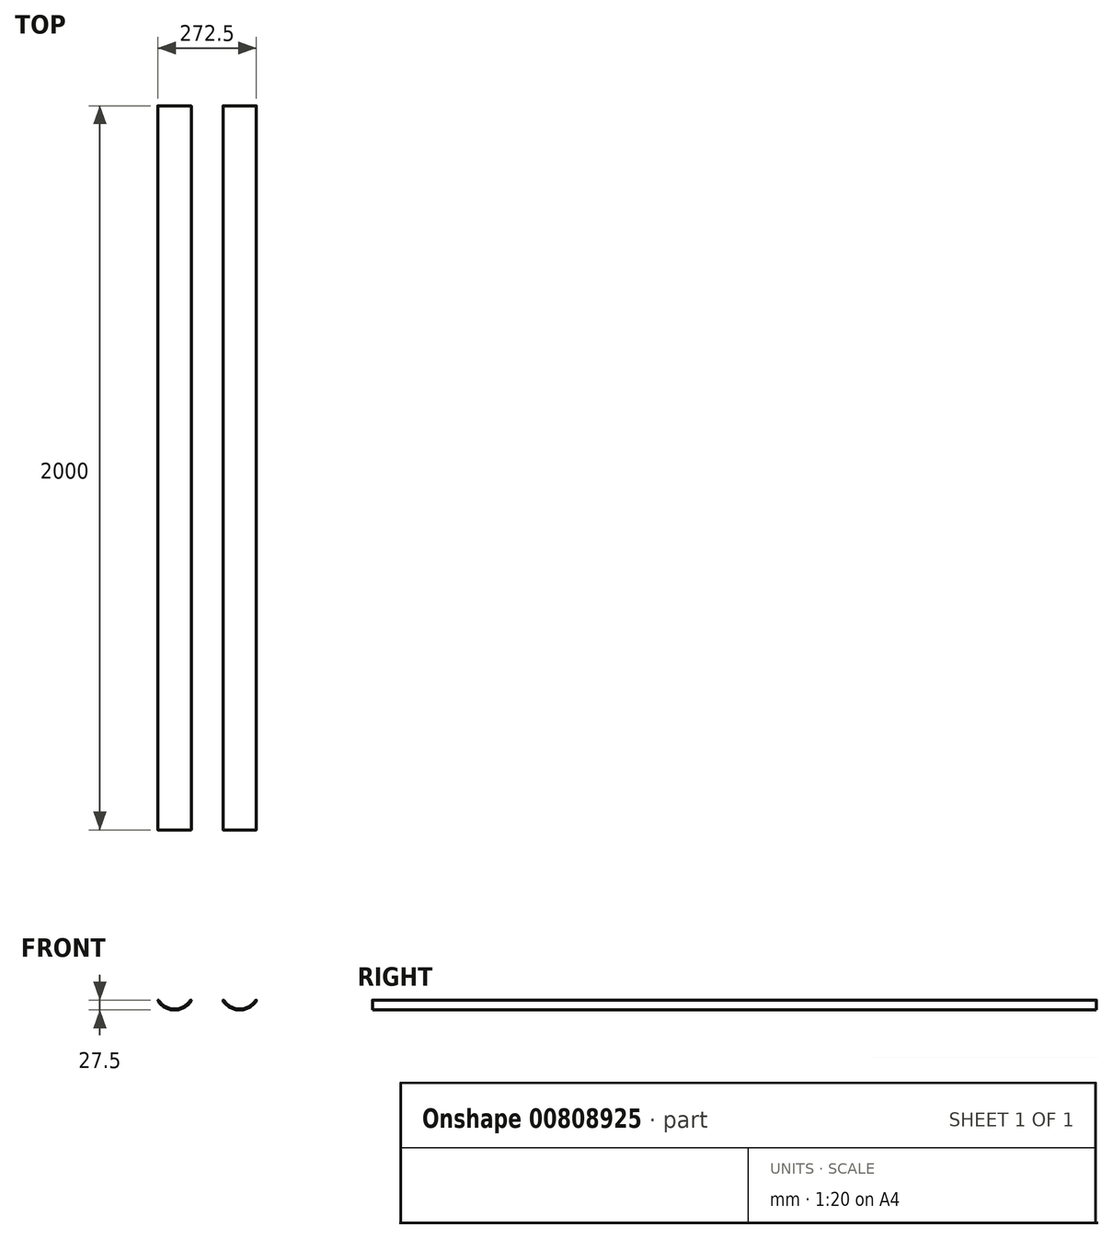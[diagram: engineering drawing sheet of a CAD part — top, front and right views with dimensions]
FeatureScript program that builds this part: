
annotation { "Feature Type Name" : "Feature", "Feature Type Description" : "" }
export const myFeature = defineFeature(function(context is Context, id is Id, definition is map)
    precondition{}
    {
        {
            var Q0;
            Q0=qCreatedBy(makeId("Front.planeOp"),FACE);
            var sketch = newSketch(context, id + "F0", { "sketchPlane" : qUnion([Q0])});
            skArc(sketch, "E0", {"start": v(0, 0) * mm, "mid": v(-45, 25) * mm, "end": v(-90, 0) * mm});
            skArc(sketch, "E1", {"start": v(0, 0) * mm, "mid": v(45, -25) * mm, "end": v(90, 0) * mm});
            skArc(sketch, "E2.1.0.0", {"start": v(180, 0) * mm, "mid": v(135, 25) * mm, "end": v(90, 0) * mm});
            skArc(sketch, "E2.1.0.1", {"start": v(180, 0) * mm, "mid": v(135, 25) * mm, "end": v(90, 0) * mm});
            skArc(sketch, "E2.1.0.2", {"start": v(180, 0) * mm, "mid": v(225, -25) * mm, "end": v(270, 0) * mm});
            skArc(sketch, "E2.2.0.0", {"start": v(360, 0) * mm, "mid": v(315, 25) * mm, "end": v(270, 0) * mm});
            skArc(sketch, "E2.2.0.1", {"start": v(360, 0) * mm, "mid": v(315, 25) * mm, "end": v(270, 0) * mm});
            skArc(sketch, "E2.2.0.2", {"start": v(360, 0) * mm, "mid": v(405, -25) * mm, "end": v(450, 0) * mm});
            skArc(sketch, "E2.3.0.0", {"start": v(540, 0) * mm, "mid": v(495, 25) * mm, "end": v(450, 0) * mm});
            skArc(sketch, "E2.3.0.1", {"start": v(540, 0) * mm, "mid": v(495, 25) * mm, "end": v(450, 0) * mm});
            skArc(sketch, "E3", {"start": v(-97.5, -9.45) * mm, "mid": v(-93.48, -4.94) * mm, "end": v(-90, 0) * mm});
            skPoint(sketch, "E4.orphan", {"position": v(900, 0) * mm});
            skArc(sketch, "E5.0.startCap", {"start": v(181.06, 0.66) * mm, "mid": v(180.66, -1.06) * mm, "end": v(178.94, -0.66) * mm});
            skArc(sketch, "E5.0.endCap", {"start": v(91.06, -0.66) * mm, "mid": v(89.34, -1.06) * mm, "end": v(88.94, 0.66) * mm});
            skArc(sketch, "E5.0.left", {"start": v(178.94, -0.66) * mm, "mid": v(135, 23.75) * mm, "end": v(91.06, -0.66) * mm});
            skArc(sketch, "E5.0.right", {"start": v(181.06, 0.66) * mm, "mid": v(135, 26.25) * mm, "end": v(88.94, 0.66) * mm});
            skArc(sketch, "E5.1.startCap", {"start": v(178.94, -0.66) * mm, "mid": v(179.34, 1.06) * mm, "end": v(181.06, 0.66) * mm});
            skArc(sketch, "E5.1.endCap", {"start": v(268.94, 0.66) * mm, "mid": v(270.66, 1.06) * mm, "end": v(271.06, -0.66) * mm});
            skArc(sketch, "E5.1.left", {"start": v(181.06, 0.66) * mm, "mid": v(225, -23.75) * mm, "end": v(268.94, 0.66) * mm});
            skArc(sketch, "E5.1.right", {"start": v(178.94, -0.66) * mm, "mid": v(225, -26.25) * mm, "end": v(271.06, -0.66) * mm});
            skArc(sketch, "E5.2.startCap", {"start": v(-1.06, -0.66) * mm, "mid": v(-0.66, 1.06) * mm, "end": v(1.06, 0.66) * mm});
            skArc(sketch, "E5.2.endCap", {"start": v(88.94, 0.66) * mm, "mid": v(90.66, 1.06) * mm, "end": v(91.06, -0.66) * mm});
            skArc(sketch, "E5.2.left", {"start": v(1.06, 0.66) * mm, "mid": v(45, -23.75) * mm, "end": v(88.94, 0.66) * mm});
            skArc(sketch, "E5.2.right", {"start": v(-1.06, -0.66) * mm, "mid": v(45, -26.25) * mm, "end": v(91.06, -0.66) * mm});
            skArc(sketch, "E5.3.startCap", {"start": v(538.94, -0.66) * mm, "mid": v(539.34, 1.06) * mm, "end": v(541.06, 0.66) * mm});
            skArc(sketch, "E5.5.startCap", {"start": v(541.06, 0.66) * mm, "mid": v(540.66, -1.06) * mm, "end": v(538.94, -0.66) * mm});
            skArc(sketch, "E5.5.endCap", {"start": v(451.06, -0.66) * mm, "mid": v(449.34, -1.06) * mm, "end": v(448.94, 0.66) * mm});
            skArc(sketch, "E5.5.left", {"start": v(538.94, -0.66) * mm, "mid": v(495, 23.75) * mm, "end": v(451.06, -0.66) * mm});
            skArc(sketch, "E5.5.right", {"start": v(541.06, 0.66) * mm, "mid": v(495, 26.25) * mm, "end": v(448.94, 0.66) * mm});
            skArc(sketch, "E5.6.startCap", {"start": v(-96.62, -10.34) * mm, "mid": v(-98.38, -10.34) * mm, "end": v(-98.38, -8.57) * mm});
            skArc(sketch, "E5.6.endCap", {"start": v(-91.06, 0.66) * mm, "mid": v(-89.34, 1.06) * mm, "end": v(-88.94, -0.66) * mm});
            skArc(sketch, "E5.6.left", {"start": v(-98.38, -8.57) * mm, "mid": v(-94.46, -4.16) * mm, "end": v(-91.06, 0.66) * mm});
            skArc(sketch, "E5.6.right", {"start": v(-96.62, -10.34) * mm, "mid": v(-92.5, -5.72) * mm, "end": v(-88.94, -0.66) * mm});
            skArc(sketch, "E5.7.startCap", {"start": v(1.06, 0.66) * mm, "mid": v(0.66, -1.06) * mm, "end": v(-1.06, -0.66) * mm});
            skArc(sketch, "E5.7.endCap", {"start": v(-88.94, -0.66) * mm, "mid": v(-90.66, -1.06) * mm, "end": v(-91.06, 0.66) * mm});
            skArc(sketch, "E5.7.left", {"start": v(-1.06, -0.66) * mm, "mid": v(-45, 23.75) * mm, "end": v(-88.94, -0.66) * mm});
            skArc(sketch, "E5.7.right", {"start": v(1.06, 0.66) * mm, "mid": v(-45, 26.25) * mm, "end": v(-91.06, 0.66) * mm});
            skArc(sketch, "E5.10.startCap", {"start": v(358.94, -0.66) * mm, "mid": v(359.34, 1.06) * mm, "end": v(361.06, 0.66) * mm});
            skArc(sketch, "E5.10.endCap", {"start": v(448.94, 0.66) * mm, "mid": v(450.66, 1.06) * mm, "end": v(451.06, -0.66) * mm});
            skArc(sketch, "E5.10.left", {"start": v(361.06, 0.66) * mm, "mid": v(405, -23.75) * mm, "end": v(448.94, 0.66) * mm});
            skArc(sketch, "E5.10.right", {"start": v(358.94, -0.66) * mm, "mid": v(405, -26.25) * mm, "end": v(451.06, -0.66) * mm});
            skArc(sketch, "E5.11.startCap", {"start": v(361.06, 0.66) * mm, "mid": v(360.66, -1.06) * mm, "end": v(358.94, -0.66) * mm});
            skArc(sketch, "E5.11.endCap", {"start": v(271.06, -0.66) * mm, "mid": v(269.34, -1.06) * mm, "end": v(268.94, 0.66) * mm});
            skArc(sketch, "E5.11.left", {"start": v(358.94, -0.66) * mm, "mid": v(315, 23.75) * mm, "end": v(271.06, -0.66) * mm});
            skArc(sketch, "E5.11.right", {"start": v(361.06, 0.66) * mm, "mid": v(315, 26.25) * mm, "end": v(268.94, 0.66) * mm});
            skArc(sketch, "E5.12.startCap", {"start": v(-1.06, -0.66) * mm, "mid": v(-0.66, 1.06) * mm, "end": v(1.06, 0.66) * mm});
            skArc(sketch, "E5.12.endCap", {"start": v(88.94, 0.66) * mm, "mid": v(90.66, 1.06) * mm, "end": v(91.06, -0.66) * mm});
            skArc(sketch, "E5.12.left", {"start": v(1.06, 0.66) * mm, "mid": v(45, -23.75) * mm, "end": v(88.94, 0.66) * mm});
            skArc(sketch, "E5.12.right", {"start": v(-1.06, -0.66) * mm, "mid": v(45, -26.25) * mm, "end": v(91.06, -0.66) * mm});
            skArc(sketch, "E5.13.startCap", {"start": v(181.06, 0.66) * mm, "mid": v(180.66, -1.06) * mm, "end": v(178.94, -0.66) * mm});
            skArc(sketch, "E5.13.endCap", {"start": v(91.06, -0.66) * mm, "mid": v(89.34, -1.06) * mm, "end": v(88.94, 0.66) * mm});
            skArc(sketch, "E5.13.left", {"start": v(178.94, -0.66) * mm, "mid": v(135, 23.75) * mm, "end": v(91.06, -0.66) * mm});
            skArc(sketch, "E5.13.right", {"start": v(181.06, 0.66) * mm, "mid": v(135, 26.25) * mm, "end": v(88.94, 0.66) * mm});
            skArc(sketch, "E5.14.startCap", {"start": v(1.06, 0.66) * mm, "mid": v(0.66, -1.06) * mm, "end": v(-1.06, -0.66) * mm});
            skArc(sketch, "E5.14.endCap", {"start": v(-88.94, -0.66) * mm, "mid": v(-90.66, -1.06) * mm, "end": v(-91.06, 0.66) * mm});
            skArc(sketch, "E5.14.left", {"start": v(-1.06, -0.66) * mm, "mid": v(-45, 23.75) * mm, "end": v(-88.94, -0.66) * mm});
            skArc(sketch, "E5.14.right", {"start": v(1.06, 0.66) * mm, "mid": v(-45, 26.25) * mm, "end": v(-91.06, 0.66) * mm});
            skArc(sketch, "E5.15.startCap", {"start": v(541.06, 0.66) * mm, "mid": v(540.66, -1.06) * mm, "end": v(538.94, -0.66) * mm});
            skArc(sketch, "E5.15.endCap", {"start": v(451.06, -0.66) * mm, "mid": v(449.34, -1.06) * mm, "end": v(448.94, 0.66) * mm});
            skArc(sketch, "E5.15.left", {"start": v(538.94, -0.66) * mm, "mid": v(495, 23.75) * mm, "end": v(451.06, -0.66) * mm});
            skArc(sketch, "E5.15.right", {"start": v(541.06, 0.66) * mm, "mid": v(495, 26.25) * mm, "end": v(448.94, 0.66) * mm});
            skArc(sketch, "E5.17.startCap", {"start": v(361.06, 0.66) * mm, "mid": v(360.66, -1.06) * mm, "end": v(358.94, -0.66) * mm});
            skArc(sketch, "E5.17.endCap", {"start": v(271.06, -0.66) * mm, "mid": v(269.34, -1.06) * mm, "end": v(268.94, 0.66) * mm});
            skArc(sketch, "E5.17.left", {"start": v(358.94, -0.66) * mm, "mid": v(315, 23.75) * mm, "end": v(271.06, -0.66) * mm});
            skArc(sketch, "E5.17.right", {"start": v(361.06, 0.66) * mm, "mid": v(315, 26.25) * mm, "end": v(268.94, 0.66) * mm});
            skSolve(sketch);
        }
        {
            var Q0;
            {var subQ5=sQuery(id+"F0.wireOp",EDGE,"E5.17.left");Q0=makeQuery(id+"F0.imprint","IMPRINT",FACE,{"disambiguationData":[TD([[makeQuery(id+"F0.imprint","IMPRINT",EDGE,{"derivedFrom":subQ5}),-1.0]])]});}
            var Q1;
            {var subQ5=sQuery(id+"F0.wireOp",EDGE,"E5.14.left");Q1=makeQuery(id+"F0.imprint","IMPRINT",FACE,{"disambiguationData":[TD([[makeQuery(id+"F0.imprint","IMPRINT",EDGE,{"derivedFrom":subQ5}),-1.0]])]});}
            var Q2;
            {var subQ5=sQuery(id+"F0.wireOp",EDGE,"E5.1.left");Q2=makeQuery(id+"F0.imprint","IMPRINT",FACE,{"disambiguationData":[TD([[makeQuery(id+"F0.imprint","IMPRINT",EDGE,{"derivedFrom":subQ5}),-1.0]])]});}
            var Q3;
            {var subQ5=sQuery(id+"F0.wireOp",EDGE,"E5.13.right");Q3=makeQuery(id+"F0.imprint","IMPRINT",FACE,{"disambiguationData":[TD([[makeQuery(id+"F0.imprint","IMPRINT",EDGE,{"derivedFrom":subQ5}),1.0]])]});}
            var Q4;
            {var subQ5=sQuery(id+"F0.wireOp",EDGE,"E5.10.left");Q4=makeQuery(id+"F0.imprint","IMPRINT",FACE,{"disambiguationData":[TD([[makeQuery(id+"F0.imprint","IMPRINT",EDGE,{"derivedFrom":subQ5}),-1.0]])]});}
            var Q5;
            {var subQ5=sQuery(id+"F0.wireOp",EDGE,"E5.15.right");Q5=makeQuery(id+"F0.imprint","IMPRINT",FACE,{"disambiguationData":[TD([[makeQuery(id+"F0.imprint","IMPRINT",EDGE,{"derivedFrom":subQ5}),1.0]])]});}
            var Q6;
            {var subQ5=sQuery(id+"F0.wireOp",EDGE,"E5.10.right");Q6=makeQuery(id+"F0.imprint","IMPRINT",FACE,{"disambiguationData":[TD([[makeQuery(id+"F0.imprint","IMPRINT",EDGE,{"derivedFrom":subQ5}),1.0]])]});}
            var Q7;
            {var subQ5=sQuery(id+"F0.wireOp",EDGE,"E5.1.right");Q7=makeQuery(id+"F0.imprint","IMPRINT",FACE,{"disambiguationData":[TD([[makeQuery(id+"F0.imprint","IMPRINT",EDGE,{"derivedFrom":subQ5}),1.0]])]});}
            var Q8;
            {var subQ0=sQuery(id+"F0.wireOp",EDGE,"E5.12.startCap");var subQ1=sQuery(id+"F0.wireOp",EDGE,"E0");var subQ2=makeQuery(id+"F0.imprint","INTERSECT",VERTEX,{"derivedFrom":[subQ1,subQ0]});Q8=makeQuery(id+"F0.imprint","IMPRINT",FACE,{"disambiguationData":[TD([[makeQuery(id+"F0.imprint","IMPRINT",EDGE,{"disambiguationData":[TD([[subQ2,-1.0]])],"derivedFrom":subQ1}),-1.0]])]});}
            var Q9;
            {var subQ5=sQuery(id+"F0.wireOp",EDGE,"E5.15.left");Q9=makeQuery(id+"F0.imprint","IMPRINT",FACE,{"disambiguationData":[TD([[makeQuery(id+"F0.imprint","IMPRINT",EDGE,{"derivedFrom":subQ5}),-1.0]])]});}
            var Q10;
            {var subQ5=sQuery(id+"F0.wireOp",EDGE,"E5.17.right");Q10=makeQuery(id+"F0.imprint","IMPRINT",FACE,{"disambiguationData":[TD([[makeQuery(id+"F0.imprint","IMPRINT",EDGE,{"derivedFrom":subQ5}),1.0]])]});}
            var Q11;
            {var subQ5=sQuery(id+"F0.wireOp",EDGE,"E5.12.left");Q11=makeQuery(id+"F0.imprint","IMPRINT",FACE,{"disambiguationData":[TD([[makeQuery(id+"F0.imprint","IMPRINT",EDGE,{"derivedFrom":subQ5}),-1.0]])]});}
            var Q12;
            {var subQ5=sQuery(id+"F0.wireOp",EDGE,"E5.12.right");Q12=makeQuery(id+"F0.imprint","IMPRINT",FACE,{"disambiguationData":[TD([[makeQuery(id+"F0.imprint","IMPRINT",EDGE,{"derivedFrom":subQ5}),1.0]])]});}
            var Q13;
            {var subQ5=sQuery(id+"F0.wireOp",EDGE,"E5.13.left");Q13=makeQuery(id+"F0.imprint","IMPRINT",FACE,{"disambiguationData":[TD([[makeQuery(id+"F0.imprint","IMPRINT",EDGE,{"derivedFrom":subQ5}),-1.0]])]});}
            var Q14;
            Q14=makeQuery(id+"F0.imprint","IMPRINT",FACE,{"disambiguationData":[TD([[makeQuery(id+"F0.imprint","IMPRINT",EDGE,{"derivedFrom":sQuery(id+"F0.wireOp",EDGE,"E5.6.startCap")}),-1.0]])]});
            var Q15;
            {var subQ0=sQuery(id+"F0.wireOp",EDGE,"E2.2.0.1");var subQ1=sQuery(id+"F0.wireOp",EDGE,"E2.1.0.2");var subQ2=makeQuery(id+"F0.imprint","INTERSECT",VERTEX,{"derivedFrom":[subQ1,subQ0]});Q15=makeQuery(id+"F0.imprint","IMPRINT",FACE,{"disambiguationData":[TD([[makeQuery(id+"F0.imprint","IMPRINT",EDGE,{"disambiguationData":[TD([[subQ2,1.0]])],"derivedFrom":subQ1}),1.0]])]});}
            var Q16;
            {var subQ0=sQuery(id+"F0.wireOp",EDGE,"E5.15.startCap");Q16=makeQuery(id+"F0.imprint","IMPRINT",FACE,{"disambiguationData":[TD([[makeQuery(id+"F0.imprint","IMPRINT",EDGE,{"derivedFrom":subQ0}),-1.0]])]});}
            var Q17;
            {var subQ0=sQuery(id+"F0.wireOp",EDGE,"E2.3.0.1");var subQ1=sQuery(id+"F0.wireOp",EDGE,"E2.2.0.2");var subQ2=makeQuery(id+"F0.imprint","INTERSECT",VERTEX,{"derivedFrom":[subQ1,subQ0]});Q17=makeQuery(id+"F0.imprint","IMPRINT",FACE,{"disambiguationData":[TD([[makeQuery(id+"F0.imprint","IMPRINT",EDGE,{"disambiguationData":[TD([[subQ2,1.0]])],"derivedFrom":subQ1}),1.0]])]});}
            var Q18;
            {var subQ0=sQuery(id+"F0.wireOp",EDGE,"E2.2.0.1");var subQ1=sQuery(id+"F0.wireOp",EDGE,"E2.1.0.2");var subQ2=makeQuery(id+"F0.imprint","INTERSECT",VERTEX,{"derivedFrom":[subQ1,subQ0]});Q18=makeQuery(id+"F0.imprint","IMPRINT",FACE,{"disambiguationData":[TD([[makeQuery(id+"F0.imprint","IMPRINT",EDGE,{"disambiguationData":[TD([[subQ2,1.0]])],"derivedFrom":subQ1}),-1.0]])]});}
            var Q19;
            {var subQ0=sQuery(id+"F0.wireOp",EDGE,"E2.3.0.1");var subQ1=sQuery(id+"F0.wireOp",EDGE,"E2.2.0.2");var subQ2=makeQuery(id+"F0.imprint","INTERSECT",VERTEX,{"derivedFrom":[subQ1,subQ0]});Q19=makeQuery(id+"F0.imprint","IMPRINT",FACE,{"disambiguationData":[TD([[makeQuery(id+"F0.imprint","IMPRINT",EDGE,{"disambiguationData":[TD([[subQ2,1.0]])],"derivedFrom":subQ1}),-1.0]])]});}
            var Q20;
            {var subQ4=sQuery(id+"F0.wireOp",EDGE,"E0");var subQ6=sQuery(id+"F0.wireOp",EDGE,"E3");var subQ7=makeQuery(id+"F0.imprint","INTERSECT",VERTEX,{"derivedFrom":[subQ4,subQ6]});Q20=makeQuery(id+"F0.imprint","IMPRINT",FACE,{"disambiguationData":[TD([[makeQuery(id+"F0.imprint","IMPRINT",EDGE,{"disambiguationData":[TD([[subQ7,1.0]])],"derivedFrom":subQ4}),1.0]])]});}
            var Q21;
            {var subQ3=sQuery(id+"F0.wireOp",EDGE,"E3");var subQ7=sQuery(id+"F0.wireOp",EDGE,"E0");var subQ9=makeQuery(id+"F0.imprint","INTERSECT",VERTEX,{"derivedFrom":[subQ7,subQ3]});Q21=makeQuery(id+"F0.imprint","IMPRINT",FACE,{"disambiguationData":[TD([[makeQuery(id+"F0.imprint","IMPRINT",EDGE,{"disambiguationData":[TD([[subQ9,1.0]])],"derivedFrom":subQ7}),-1.0]])]});}
            var Q22;
            {var subQ0=sQuery(id+"F0.wireOp",EDGE,"E2.1.0.1");var subQ1=sQuery(id+"F0.wireOp",EDGE,"E1");var subQ2=makeQuery(id+"F0.imprint","INTERSECT",VERTEX,{"derivedFrom":[subQ1,subQ0]});Q22=makeQuery(id+"F0.imprint","IMPRINT",FACE,{"disambiguationData":[TD([[makeQuery(id+"F0.imprint","IMPRINT",EDGE,{"disambiguationData":[TD([[subQ2,1.0]])],"derivedFrom":subQ1}),-1.0]])]});}
            var Q23;
            {var subQ0=sQuery(id+"F0.wireOp",EDGE,"E2.1.0.1");var subQ1=sQuery(id+"F0.wireOp",EDGE,"E1");var subQ2=makeQuery(id+"F0.imprint","INTERSECT",VERTEX,{"derivedFrom":[subQ1,subQ0]});Q23=makeQuery(id+"F0.imprint","IMPRINT",FACE,{"disambiguationData":[TD([[makeQuery(id+"F0.imprint","IMPRINT",EDGE,{"disambiguationData":[TD([[subQ2,1.0]])],"derivedFrom":subQ1}),1.0]])]});}
            var Q24;
            {var subQ0=sQuery(id+"F0.wireOp",EDGE,"E2.1.0.2");var subQ1=sQuery(id+"F0.wireOp",EDGE,"E2.1.0.1");var subQ2=makeQuery(id+"F0.imprint","INTERSECT",VERTEX,{"derivedFrom":[subQ1,subQ0]});Q24=makeQuery(id+"F0.imprint","IMPRINT",FACE,{"disambiguationData":[TD([[makeQuery(id+"F0.imprint","IMPRINT",EDGE,{"disambiguationData":[TD([[subQ2,-1.0]])],"derivedFrom":subQ1}),1.0]])]});}
            var Q25;
            {var subQ0=sQuery(id+"F0.wireOp",EDGE,"E2.2.0.2");var subQ1=sQuery(id+"F0.wireOp",EDGE,"E2.2.0.1");var subQ2=makeQuery(id+"F0.imprint","INTERSECT",VERTEX,{"derivedFrom":[subQ1,subQ0]});Q25=makeQuery(id+"F0.imprint","IMPRINT",FACE,{"disambiguationData":[TD([[makeQuery(id+"F0.imprint","IMPRINT",EDGE,{"disambiguationData":[TD([[subQ2,-1.0]])],"derivedFrom":subQ1}),1.0]])]});}
            var Q26;
            {var subQ0=sQuery(id+"F0.wireOp",EDGE,"E2.1.0.2");var subQ1=sQuery(id+"F0.wireOp",EDGE,"E2.1.0.1");var subQ2=makeQuery(id+"F0.imprint","INTERSECT",VERTEX,{"derivedFrom":[subQ1,subQ0]});Q26=makeQuery(id+"F0.imprint","IMPRINT",FACE,{"disambiguationData":[TD([[makeQuery(id+"F0.imprint","IMPRINT",EDGE,{"disambiguationData":[TD([[subQ2,-1.0]])],"derivedFrom":subQ1}),-1.0]])]});}
            var Q27;
            {var subQ0=sQuery(id+"F0.wireOp",EDGE,"E2.2.0.2");var subQ1=sQuery(id+"F0.wireOp",EDGE,"E2.2.0.1");var subQ2=makeQuery(id+"F0.imprint","INTERSECT",VERTEX,{"derivedFrom":[subQ1,subQ0]});Q27=makeQuery(id+"F0.imprint","IMPRINT",FACE,{"disambiguationData":[TD([[makeQuery(id+"F0.imprint","IMPRINT",EDGE,{"disambiguationData":[TD([[subQ2,-1.0]])],"derivedFrom":subQ1}),-1.0]])]});}
            var Q28;
            {var subQ0=sQuery(id+"F0.wireOp",EDGE,"E1");var subQ1=sQuery(id+"F0.wireOp",EDGE,"E0");var subQ2=makeQuery(id+"F0.imprint","INTERSECT",VERTEX,{"derivedFrom":[subQ1,subQ0]});Q28=makeQuery(id+"F0.imprint","IMPRINT",FACE,{"disambiguationData":[TD([[makeQuery(id+"F0.imprint","IMPRINT",EDGE,{"disambiguationData":[TD([[subQ2,-1.0]])],"derivedFrom":subQ1}),-1.0]])]});}
            var Q29;
            {var subQ0=sQuery(id+"F0.wireOp",EDGE,"E1");var subQ1=sQuery(id+"F0.wireOp",EDGE,"E0");var subQ2=makeQuery(id+"F0.imprint","INTERSECT",VERTEX,{"derivedFrom":[subQ1,subQ0]});Q29=makeQuery(id+"F0.imprint","IMPRINT",FACE,{"disambiguationData":[TD([[makeQuery(id+"F0.imprint","IMPRINT",EDGE,{"disambiguationData":[TD([[subQ2,-1.0]])],"derivedFrom":subQ1}),1.0]])]});}
            extrude(context, id + "F1", {"entities" : qUnion([Q0, Q1, Q2, Q3, Q4, Q5, Q6, Q7, Q8, Q9, Q10, Q11, Q12, Q13, Q14, Q15, Q16, Q17, Q18, Q19, Q20, Q21, Q22, Q23, Q24, Q25, Q26, Q27, Q28, Q29]), "depth" : 2000 * mm, "offsetDistance" : 25 * mm});
        }
    });
